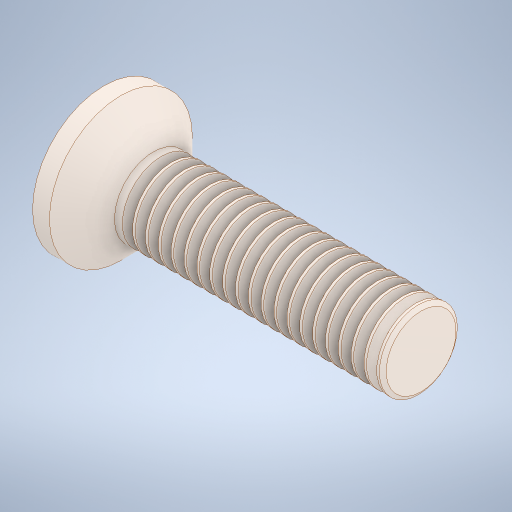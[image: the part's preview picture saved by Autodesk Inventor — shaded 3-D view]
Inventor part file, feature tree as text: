
AUTODESK INVENTOR PART (.ipt)
format: ipt  version: 2023 (Build 270158000, 158)  size: 395,264 bytes
history: mixed  units: mm
features: other x2, extrude x1, sketch x1, imported_body x1
ambient origin geometry x8: Origin, YZ Plane, XZ Plane, XY Plane, X Axis, Y Axis, Z Axis, Center Point
bodies: Body1 (imported_parasolid)
feature tree (5):
  other  "Sólido1"
  extrude  "Extrusão1"  Depth=8.0mm TaperAngle=0.0deg
  sketch  "Esboço1"  dims[d0=3.0mm d1=8.0mm d2=0.0mm]
  other  "ThdSchPat"
  imported_body  NMx_Import_Brep_tag  [imported B-rep: ~79 faces, bbox_mm=[12.704589, 3.198662, 4.349331]]
